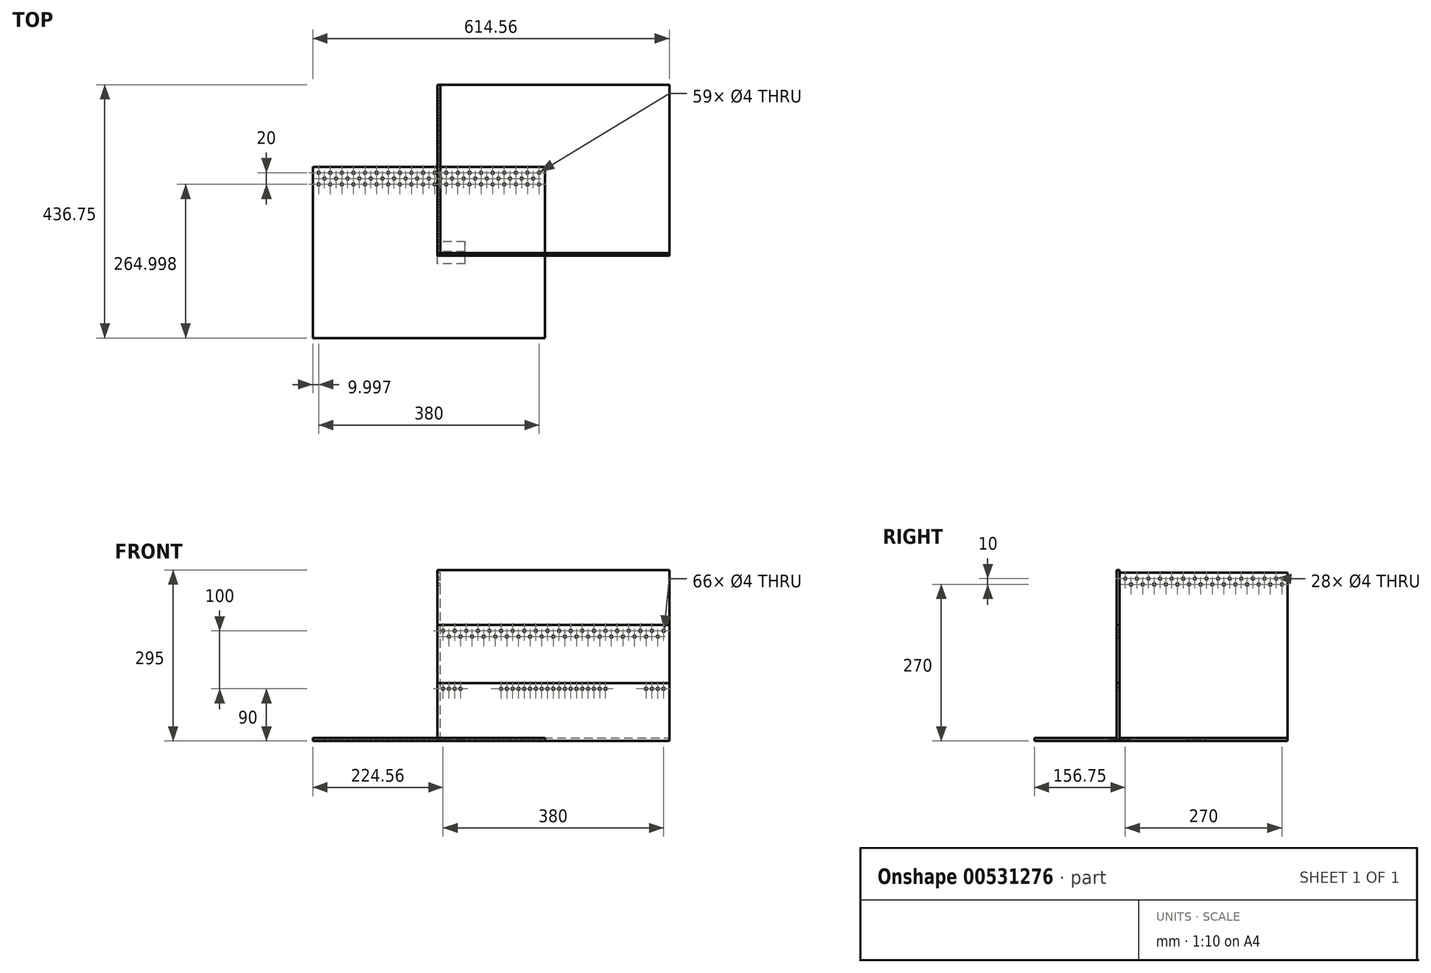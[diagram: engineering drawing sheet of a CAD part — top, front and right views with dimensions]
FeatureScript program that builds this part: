
annotation { "Feature Type Name" : "Feature", "Feature Type Description" : "" }
export const myFeature = defineFeature(function(context is Context, id is Id, definition is map)
    precondition{}
    {
        {
            var Q0;
            Q0=qCreatedBy(makeId("Front.planeOp"),FACE);
            var sketch = newSketch(context, id + "F0", { "sketchPlane" : qUnion([Q0])});
            skLineSegment(sketch, "E0.bottom", {"start": v(0, 0) * mm, "end": v(400, 0) * mm});
            skLineSegment(sketch, "E0.top", {"start": v(0, 100) * mm, "end": v(400, 100) * mm});
            skLineSegment(sketch, "E0.left", {"start": v(0, 0) * mm, "end": v(0, 100) * mm});
            skLineSegment(sketch, "E0.right", {"start": v(400, 0) * mm, "end": v(400, 100) * mm});
            skCircle(sketch, "E1", {"center": v(10, 90) * mm, "radius": 2 * mm});
            skCircle(sketch, "E2.1.0.0", {"center": v(20, 90) * mm, "radius": 2 * mm});
            skCircle(sketch, "E2.2.0.0", {"center": v(30, 90) * mm, "radius": 2 * mm});
            skCircle(sketch, "E2.3.0.0", {"center": v(40, 90) * mm, "radius": 2 * mm});
            skCircle(sketch, "E2.10.0.0", {"center": v(110, 90) * mm, "radius": 2 * mm});
            skCircle(sketch, "E2.11.0.0", {"center": v(120, 90) * mm, "radius": 2 * mm});
            skCircle(sketch, "E2.12.0.0", {"center": v(130, 90) * mm, "radius": 2 * mm});
            skCircle(sketch, "E2.13.0.0", {"center": v(140, 90) * mm, "radius": 2 * mm});
            skCircle(sketch, "E2.14.0.0", {"center": v(150, 90) * mm, "radius": 2 * mm});
            skCircle(sketch, "E2.15.0.0", {"center": v(160, 90) * mm, "radius": 2 * mm});
            skCircle(sketch, "E2.16.0.0", {"center": v(170, 90) * mm, "radius": 2 * mm});
            skCircle(sketch, "E2.17.0.0", {"center": v(180, 90) * mm, "radius": 2 * mm});
            skCircle(sketch, "E2.18.0.0", {"center": v(190, 90) * mm, "radius": 2 * mm});
            skCircle(sketch, "E2.19.0.0", {"center": v(200, 90) * mm, "radius": 2 * mm});
            skCircle(sketch, "E2.20.0.0", {"center": v(210, 90) * mm, "radius": 2 * mm});
            skCircle(sketch, "E2.21.0.0", {"center": v(220, 90) * mm, "radius": 2 * mm});
            skCircle(sketch, "E2.22.0.0", {"center": v(230, 90) * mm, "radius": 2 * mm});
            skCircle(sketch, "E2.23.0.0", {"center": v(240, 90) * mm, "radius": 2 * mm});
            skCircle(sketch, "E2.24.0.0", {"center": v(250, 90) * mm, "radius": 2 * mm});
            skCircle(sketch, "E2.25.0.0", {"center": v(260, 90) * mm, "radius": 2 * mm});
            skCircle(sketch, "E2.26.0.0", {"center": v(270, 90) * mm, "radius": 2 * mm});
            skCircle(sketch, "E2.27.0.0", {"center": v(280, 90) * mm, "radius": 2 * mm});
            skCircle(sketch, "E2.28.0.0", {"center": v(290, 90) * mm, "radius": 2 * mm});
            skCircle(sketch, "E2.35.0.0", {"center": v(360, 90) * mm, "radius": 2 * mm});
            skCircle(sketch, "E2.36.0.0", {"center": v(370, 90) * mm, "radius": 2 * mm});
            skCircle(sketch, "E2.37.0.0", {"center": v(380, 90) * mm, "radius": 2 * mm});
            skCircle(sketch, "E2.38.0.0", {"center": v(390, 90) * mm, "radius": 2 * mm});
            skLineSegment(sketch, "E2.direction1", {"start": v(10, 90) * mm, "end": v(20, 90) * mm, "construction": true});
            skLineSegment(sketch, "E3.top", {"start": v(50, 81) * mm, "end": v(95, 81) * mm, "construction": true});
            skLineSegment(sketch, "E3.left", {"start": v(50, 100) * mm, "end": v(50, 81) * mm, "construction": true});
            skLineSegment(sketch, "E3.right", {"start": v(95, 100) * mm, "end": v(95, 81) * mm, "construction": true});
            skLineSegment(sketch, "E4.top", {"start": v(350, 81) * mm, "end": v(305, 81) * mm, "construction": true});
            skLineSegment(sketch, "E4.left", {"start": v(350, 100) * mm, "end": v(350, 81) * mm, "construction": true});
            skLineSegment(sketch, "E4.right", {"start": v(305, 100) * mm, "end": v(305, 81) * mm, "construction": true});
            skSolve(sketch);
        }
        {
            var Q0;
            Q0=makeQuery(id+"F0.imprint","IMPRINT",FACE,{"disambiguationData":[TD([[makeQuery(id+"F0.imprint","IMPRINT",EDGE,{"derivedFrom":sQuery(id+"F0.wireOp",EDGE,"E0.bottom")}),1.0]])]});
            extrude(context, id + "F1", {"entities" : qUnion([Q0]), "depth" : 5 * mm, "offsetDistance" : 25 * mm});
        }
        {
            var Q0;
            Q0=qCreatedBy(makeId("Front.planeOp"),FACE);
            var sketch = newSketch(context, id + "F2", { "sketchPlane" : qUnion([Q0])});
            skLineSegment(sketch, "E5.bottom", {"start": v(0, 0) * mm, "end": v(400, 0) * mm});
            skLineSegment(sketch, "E5.top", {"start": v(0, 200) * mm, "end": v(400, 200) * mm});
            skLineSegment(sketch, "E5.left", {"start": v(0, 0) * mm, "end": v(0, 200) * mm});
            skLineSegment(sketch, "E5.right", {"start": v(400, 0) * mm, "end": v(400, 200) * mm});
            skCircle(sketch, "E6", {"center": v(10, 190) * mm, "radius": 2 * mm});
            skCircle(sketch, "E7", {"center": v(20, 180) * mm, "radius": 2 * mm});
            skCircle(sketch, "E8.1.0.0", {"center": v(30, 190) * mm, "radius": 2 * mm});
            skCircle(sketch, "E8.2.0.0", {"center": v(50, 190) * mm, "radius": 2 * mm});
            skCircle(sketch, "E8.3.0.0", {"center": v(70, 190) * mm, "radius": 2 * mm});
            skCircle(sketch, "E8.4.0.0", {"center": v(90, 190) * mm, "radius": 2 * mm});
            skCircle(sketch, "E8.5.0.0", {"center": v(110, 190) * mm, "radius": 2 * mm});
            skCircle(sketch, "E8.6.0.0", {"center": v(130, 190) * mm, "radius": 2 * mm});
            skCircle(sketch, "E8.7.0.0", {"center": v(150, 190) * mm, "radius": 2 * mm});
            skCircle(sketch, "E8.8.0.0", {"center": v(170, 190) * mm, "radius": 2 * mm});
            skCircle(sketch, "E8.9.0.0", {"center": v(190, 190) * mm, "radius": 2 * mm});
            skCircle(sketch, "E8.10.0.0", {"center": v(210, 190) * mm, "radius": 2 * mm});
            skCircle(sketch, "E8.11.0.0", {"center": v(230, 190) * mm, "radius": 2 * mm});
            skCircle(sketch, "E8.12.0.0", {"center": v(250, 190) * mm, "radius": 2 * mm});
            skCircle(sketch, "E8.13.0.0", {"center": v(270, 190) * mm, "radius": 2 * mm});
            skCircle(sketch, "E8.14.0.0", {"center": v(290, 190) * mm, "radius": 2 * mm});
            skCircle(sketch, "E8.15.0.0", {"center": v(310, 190) * mm, "radius": 2 * mm});
            skCircle(sketch, "E8.16.0.0", {"center": v(330, 190) * mm, "radius": 2 * mm});
            skCircle(sketch, "E8.17.0.0", {"center": v(350, 190) * mm, "radius": 2 * mm});
            skCircle(sketch, "E8.18.0.0", {"center": v(370, 190) * mm, "radius": 2 * mm});
            skCircle(sketch, "E8.19.0.0", {"center": v(390, 190) * mm, "radius": 2 * mm});
            skLineSegment(sketch, "E8.direction1", {"start": v(10, 190) * mm, "end": v(30, 190) * mm, "construction": true});
            skCircle(sketch, "E9.1.0.0", {"center": v(40, 180) * mm, "radius": 2 * mm});
            skCircle(sketch, "E9.2.0.0", {"center": v(60, 180) * mm, "radius": 2 * mm});
            skCircle(sketch, "E9.3.0.0", {"center": v(80, 180) * mm, "radius": 2 * mm});
            skCircle(sketch, "E9.4.0.0", {"center": v(100, 180) * mm, "radius": 2 * mm});
            skCircle(sketch, "E9.5.0.0", {"center": v(120, 180) * mm, "radius": 2 * mm});
            skCircle(sketch, "E9.6.0.0", {"center": v(140, 180) * mm, "radius": 2 * mm});
            skCircle(sketch, "E9.7.0.0", {"center": v(160, 180) * mm, "radius": 2 * mm});
            skCircle(sketch, "E9.8.0.0", {"center": v(180, 180) * mm, "radius": 2 * mm});
            skCircle(sketch, "E9.9.0.0", {"center": v(200, 180) * mm, "radius": 2 * mm});
            skCircle(sketch, "E9.10.0.0", {"center": v(220, 180) * mm, "radius": 2 * mm});
            skCircle(sketch, "E9.11.0.0", {"center": v(240, 180) * mm, "radius": 2 * mm});
            skCircle(sketch, "E9.12.0.0", {"center": v(260, 180) * mm, "radius": 2 * mm});
            skCircle(sketch, "E9.13.0.0", {"center": v(280, 180) * mm, "radius": 2 * mm});
            skCircle(sketch, "E9.14.0.0", {"center": v(300, 180) * mm, "radius": 2 * mm});
            skCircle(sketch, "E9.15.0.0", {"center": v(320, 180) * mm, "radius": 2 * mm});
            skCircle(sketch, "E9.16.0.0", {"center": v(340, 180) * mm, "radius": 2 * mm});
            skCircle(sketch, "E9.17.0.0", {"center": v(360, 180) * mm, "radius": 2 * mm});
            skCircle(sketch, "E9.18.0.0", {"center": v(380, 180) * mm, "radius": 2 * mm});
            skLineSegment(sketch, "E9.direction1", {"start": v(20, 180) * mm, "end": v(40, 180) * mm, "construction": true});
            skSolve(sketch);
        }
        {
            var Q0;
            Q0 = qSketchRegion(id + "F2", true);
            extrude(context, id + "F3", {"entities" : qUnion([Q0]), "depth" : 5 * mm, "offsetDistance" : 25 * mm});
        }
        {
            var Q0;
            Q0=qCreatedBy(makeId("Right.planeOp"),FACE);
            var sketch = newSketch(context, id + "F4", { "sketchPlane" : qUnion([Q0])});
            skLineSegment(sketch, "E10.bottom", {"start": v(0, 0) * mm, "end": v(290, 0) * mm});
            skLineSegment(sketch, "E10.top", {"start": v(0, 290) * mm, "end": v(290, 290) * mm});
            skLineSegment(sketch, "E10.left", {"start": v(0, 0) * mm, "end": v(0, 290) * mm});
            skLineSegment(sketch, "E10.right", {"start": v(290, 0) * mm, "end": v(290, 290) * mm});
            skCircle(sketch, "E11", {"center": v(10, 280) * mm, "radius": 2 * mm});
            skCircle(sketch, "E12", {"center": v(20, 270) * mm, "radius": 2 * mm});
            skCircle(sketch, "E13.1.0.0", {"center": v(30, 280) * mm, "radius": 2 * mm});
            skCircle(sketch, "E13.2.0.0", {"center": v(50, 280) * mm, "radius": 2 * mm});
            skCircle(sketch, "E13.3.0.0", {"center": v(70, 280) * mm, "radius": 2 * mm});
            skCircle(sketch, "E13.4.0.0", {"center": v(90, 280) * mm, "radius": 2 * mm});
            skCircle(sketch, "E13.5.0.0", {"center": v(110, 280) * mm, "radius": 2 * mm});
            skCircle(sketch, "E13.6.0.0", {"center": v(130, 280) * mm, "radius": 2 * mm});
            skCircle(sketch, "E13.7.0.0", {"center": v(150, 280) * mm, "radius": 2 * mm});
            skCircle(sketch, "E13.8.0.0", {"center": v(170, 280) * mm, "radius": 2 * mm});
            skCircle(sketch, "E13.9.0.0", {"center": v(190, 280) * mm, "radius": 2 * mm});
            skCircle(sketch, "E13.10.0.0", {"center": v(210, 280) * mm, "radius": 2 * mm});
            skCircle(sketch, "E13.11.0.0", {"center": v(230, 280) * mm, "radius": 2 * mm});
            skCircle(sketch, "E13.12.0.0", {"center": v(250, 280) * mm, "radius": 2 * mm});
            skCircle(sketch, "E13.13.0.0", {"center": v(270, 280) * mm, "radius": 2 * mm});
            skLineSegment(sketch, "E13.direction1", {"start": v(10, 280) * mm, "end": v(30, 280) * mm, "construction": true});
            skCircle(sketch, "E14.1.0.0", {"center": v(40, 270) * mm, "radius": 2 * mm});
            skCircle(sketch, "E14.2.0.0", {"center": v(60, 270) * mm, "radius": 2 * mm});
            skCircle(sketch, "E14.3.0.0", {"center": v(80, 270) * mm, "radius": 2 * mm});
            skCircle(sketch, "E14.4.0.0", {"center": v(100, 270) * mm, "radius": 2 * mm});
            skCircle(sketch, "E14.5.0.0", {"center": v(120, 270) * mm, "radius": 2 * mm});
            skCircle(sketch, "E14.6.0.0", {"center": v(140, 270) * mm, "radius": 2 * mm});
            skCircle(sketch, "E14.7.0.0", {"center": v(160, 270) * mm, "radius": 2 * mm});
            skCircle(sketch, "E14.8.0.0", {"center": v(180, 270) * mm, "radius": 2 * mm});
            skCircle(sketch, "E14.9.0.0", {"center": v(200, 270) * mm, "radius": 2 * mm});
            skCircle(sketch, "E14.10.0.0", {"center": v(220, 270) * mm, "radius": 2 * mm});
            skCircle(sketch, "E14.11.0.0", {"center": v(240, 270) * mm, "radius": 2 * mm});
            skCircle(sketch, "E14.12.0.0", {"center": v(260, 270) * mm, "radius": 2 * mm});
            skCircle(sketch, "E14.13.0.0", {"center": v(280, 270) * mm, "radius": 2 * mm});
            skLineSegment(sketch, "E14.direction1", {"start": v(20, 270) * mm, "end": v(40, 270) * mm, "construction": true});
            skSolve(sketch);
        }
        {
            var Q0;
            Q0 = qSketchRegion(id + "F4", true);
            extrude(context, id + "F5", {"entities" : qUnion([Q0]), "depth" : 5 * mm, "offsetDistance" : 25 * mm});
        }
        {
            var Q0;
            Q0=qCreatedBy(makeId("Top.planeOp"),FACE);
            var sketch = newSketch(context, id + "F6", { "sketchPlane" : qUnion([Q0])});
            skLineSegment(sketch, "E15.bottom", {"start": v(0, 0) * mm, "end": v(400, 0) * mm});
            skLineSegment(sketch, "E15.top", {"start": v(0, 290) * mm, "end": v(400, 290) * mm});
            skLineSegment(sketch, "E15.left", {"start": v(0, 0) * mm, "end": v(0, 290) * mm});
            skLineSegment(sketch, "E15.right", {"start": v(400, 0) * mm, "end": v(400, 290) * mm});
            skSolve(sketch);
        }
        {
            var Q0;
            Q0 = qSketchRegion(id + "F6", true);
            extrude(context, id + "F7", {"entities" : qUnion([Q0]), "depth" : 5 * mm, "offsetDistance" : 25 * mm});
        }
        {
            var Q0;
            Q0=qCreatedBy(makeId("Front.planeOp"),FACE);
            var sketch = newSketch(context, id + "F8", { "sketchPlane" : qUnion([Q0])});
            skLineSegment(sketch, "E16.bottom", {"start": v(0, 0) * mm, "end": v(400, 0) * mm});
            skLineSegment(sketch, "E16.top", {"start": v(0, 295) * mm, "end": v(400, 295) * mm});
            skLineSegment(sketch, "E16.left", {"start": v(0, 0) * mm, "end": v(0, 295) * mm});
            skLineSegment(sketch, "E16.right", {"start": v(400, 0) * mm, "end": v(400, 295) * mm});
            skSolve(sketch);
        }
        {
            var Q0;
            Q0 = qSketchRegion(id + "F8", true);
            extrude(context, id + "F9", {"entities" : qUnion([Q0]), "depth" : 5 * mm, "offsetDistance" : 25 * mm});
        }
        {
            var Q0;
            Q0=qCreatedBy(makeId("Top.planeOp"),FACE);
            var sketch = newSketch(context, id + "F10", { "sketchPlane" : qUnion([Q0])});
            skLineSegment(sketch, "E17.bottom", {"start": v(-214.56, 148.25) * mm, "end": v(185.44, 148.25) * mm});
            skLineSegment(sketch, "E17.top", {"start": v(-214.56, -146.75) * mm, "end": v(185.44, -146.75) * mm});
            skLineSegment(sketch, "E17.left", {"start": v(-214.56, 148.25) * mm, "end": v(-214.56, -146.75) * mm});
            skLineSegment(sketch, "E17.right", {"start": v(185.44, 148.25) * mm, "end": v(185.44, -146.75) * mm});
            skCircle(sketch, "E18", {"center": v(-204.56, 138.25) * mm, "radius": 2 * mm});
            skCircle(sketch, "E19", {"center": v(-194.56, 128.25) * mm, "radius": 2 * mm});
            skCircle(sketch, "E20.1.0.0", {"center": v(-184.56, 138.25) * mm, "radius": 2 * mm});
            skCircle(sketch, "E20.2.0.0", {"center": v(-164.56, 138.25) * mm, "radius": 2 * mm});
            skCircle(sketch, "E20.3.0.0", {"center": v(-144.56, 138.25) * mm, "radius": 2 * mm});
            skCircle(sketch, "E20.4.0.0", {"center": v(-124.56, 138.25) * mm, "radius": 2 * mm});
            skCircle(sketch, "E20.5.0.0", {"center": v(-104.56, 138.25) * mm, "radius": 2 * mm});
            skCircle(sketch, "E20.6.0.0", {"center": v(-84.56, 138.25) * mm, "radius": 2 * mm});
            skCircle(sketch, "E20.7.0.0", {"center": v(-64.56, 138.25) * mm, "radius": 2 * mm});
            skCircle(sketch, "E20.8.0.0", {"center": v(-44.56, 138.25) * mm, "radius": 2 * mm});
            skCircle(sketch, "E20.9.0.0", {"center": v(-24.56, 138.25) * mm, "radius": 2 * mm});
            skCircle(sketch, "E20.10.0.0", {"center": v(-4.56, 138.25) * mm, "radius": 2 * mm});
            skCircle(sketch, "E20.11.0.0", {"center": v(15.44, 138.25) * mm, "radius": 2 * mm});
            skCircle(sketch, "E20.12.0.0", {"center": v(35.44, 138.25) * mm, "radius": 2 * mm});
            skCircle(sketch, "E20.13.0.0", {"center": v(55.44, 138.25) * mm, "radius": 2 * mm});
            skCircle(sketch, "E20.14.0.0", {"center": v(75.44, 138.25) * mm, "radius": 2 * mm});
            skLineSegment(sketch, "E20.direction1", {"start": v(-204.56, 138.25) * mm, "end": v(-184.56, 138.25) * mm, "construction": true});
            skCircle(sketch, "E21.1.0.0", {"center": v(-174.56, 128.25) * mm, "radius": 2 * mm});
            skCircle(sketch, "E21.2.0.0", {"center": v(-154.56, 128.25) * mm, "radius": 2 * mm});
            skCircle(sketch, "E21.3.0.0", {"center": v(-134.56, 128.25) * mm, "radius": 2 * mm});
            skCircle(sketch, "E21.4.0.0", {"center": v(-114.56, 128.25) * mm, "radius": 2 * mm});
            skCircle(sketch, "E21.5.0.0", {"center": v(-94.56, 128.25) * mm, "radius": 2 * mm});
            skCircle(sketch, "E21.6.0.0", {"center": v(-74.56, 128.25) * mm, "radius": 2 * mm});
            skCircle(sketch, "E21.7.0.0", {"center": v(-54.56, 128.25) * mm, "radius": 2 * mm});
            skCircle(sketch, "E21.8.0.0", {"center": v(-34.56, 128.25) * mm, "radius": 2 * mm});
            skCircle(sketch, "E21.9.0.0", {"center": v(-14.56, 128.25) * mm, "radius": 2 * mm});
            skCircle(sketch, "E21.10.0.0", {"center": v(5.44, 128.25) * mm, "radius": 2 * mm});
            skCircle(sketch, "E21.11.0.0", {"center": v(25.44, 128.25) * mm, "radius": 2 * mm});
            skCircle(sketch, "E21.12.0.0", {"center": v(45.44, 128.25) * mm, "radius": 2 * mm});
            skCircle(sketch, "E21.13.0.0", {"center": v(65.44, 128.25) * mm, "radius": 2 * mm});
            skLineSegment(sketch, "E21.direction1", {"start": v(-194.56, 128.25) * mm, "end": v(-174.56, 128.25) * mm, "construction": true});
            skCircle(sketch, "E22.0.15.0", {"center": v(95.44, 138.25) * mm, "radius": 2 * mm});
            skCircle(sketch, "E22.0.16.0", {"center": v(115.44, 138.25) * mm, "radius": 2 * mm});
            skCircle(sketch, "E22.0.17.0", {"center": v(135.44, 138.25) * mm, "radius": 2 * mm});
            skCircle(sketch, "E22.0.18.0", {"center": v(155.44, 138.25) * mm, "radius": 2 * mm});
            skCircle(sketch, "E22.0.19.0", {"center": v(175.44, 138.25) * mm, "radius": 2 * mm});
            skCircle(sketch, "E23.0.14.0", {"center": v(85.44, 128.25) * mm, "radius": 2 * mm});
            skCircle(sketch, "E23.0.15.0", {"center": v(105.44, 128.25) * mm, "radius": 2 * mm});
            skCircle(sketch, "E23.0.16.0", {"center": v(125.44, 128.25) * mm, "radius": 2 * mm});
            skCircle(sketch, "E23.0.17.0", {"center": v(145.44, 128.25) * mm, "radius": 2 * mm});
            skCircle(sketch, "E23.0.18.0", {"center": v(165.44, 128.25) * mm, "radius": 2 * mm});
            skCircle(sketch, "E24", {"center": v(-204.56, 118.25) * mm, "radius": 2 * mm});
            skCircle(sketch, "E25.1.0.0", {"center": v(-184.56, 118.25) * mm, "radius": 2 * mm});
            skCircle(sketch, "E25.2.0.0", {"center": v(-164.56, 118.25) * mm, "radius": 2 * mm});
            skCircle(sketch, "E25.3.0.0", {"center": v(-144.56, 118.25) * mm, "radius": 2 * mm});
            skCircle(sketch, "E25.4.0.0", {"center": v(-124.56, 118.25) * mm, "radius": 2 * mm});
            skCircle(sketch, "E25.5.0.0", {"center": v(-104.56, 118.25) * mm, "radius": 2 * mm});
            skCircle(sketch, "E25.6.0.0", {"center": v(-84.56, 118.25) * mm, "radius": 2 * mm});
            skCircle(sketch, "E25.7.0.0", {"center": v(-64.56, 118.25) * mm, "radius": 2 * mm});
            skCircle(sketch, "E25.8.0.0", {"center": v(-44.56, 118.25) * mm, "radius": 2 * mm});
            skCircle(sketch, "E25.9.0.0", {"center": v(-24.56, 118.25) * mm, "radius": 2 * mm});
            skCircle(sketch, "E25.10.0.0", {"center": v(-4.56, 118.25) * mm, "radius": 2 * mm});
            skCircle(sketch, "E25.11.0.0", {"center": v(15.44, 118.25) * mm, "radius": 2 * mm});
            skCircle(sketch, "E25.12.0.0", {"center": v(35.44, 118.25) * mm, "radius": 2 * mm});
            skCircle(sketch, "E25.13.0.0", {"center": v(55.44, 118.25) * mm, "radius": 2 * mm});
            skCircle(sketch, "E25.14.0.0", {"center": v(75.44, 118.25) * mm, "radius": 2 * mm});
            skCircle(sketch, "E25.15.0.0", {"center": v(95.44, 118.25) * mm, "radius": 2 * mm});
            skCircle(sketch, "E25.16.0.0", {"center": v(115.44, 118.25) * mm, "radius": 2 * mm});
            skCircle(sketch, "E25.17.0.0", {"center": v(135.44, 118.25) * mm, "radius": 2 * mm});
            skCircle(sketch, "E25.18.0.0", {"center": v(155.44, 118.25) * mm, "radius": 2 * mm});
            skCircle(sketch, "E25.19.0.0", {"center": v(175.44, 118.25) * mm, "radius": 2 * mm});
            skLineSegment(sketch, "E25.direction1", {"start": v(-204.56, 118.25) * mm, "end": v(-184.56, 118.25) * mm, "construction": true});
            skSolve(sketch);
        }
        {
            var Q0;
            Q0 = qSketchRegion(id + "F10", true);
            extrude(context, id + "F11", {"entities" : qUnion([Q0]), "depth" : 5 * mm, "offsetDistance" : 25 * mm});
        }
        {
            var Q0;
            Q0=qCreatedBy(makeId("Right.planeOp"),FACE);
            var sketch = newSketch(context, id + "F12", { "sketchPlane" : qUnion([Q0])});
            skLineSegment(sketch, "E26.bottom", {"start": v(-18.4, 0) * mm, "end": v(19.6, 0) * mm});
            skLineSegment(sketch, "E26.top", {"start": v(-12.66, 3) * mm, "end": v(-2.3, 3) * mm});
            skLineSegment(sketch, "E26.left", {"start": v(-18.4, 0) * mm, "end": v(-18.4, 0.76) * mm});
            skLineSegment(sketch, "E26.right", {"start": v(19.6, 0) * mm, "end": v(19.6, 0.76) * mm});
            skArc(sketch, "E27.trimOffspring", {"start": v(2.3, 3) * mm, "mid": v(0, 4.5) * mm, "end": v(-2.3, 3) * mm});
            skLineSegment(sketch, "E28", {"start": v(-17.68, 1.71) * mm, "end": v(-14.1, 2.79) * mm});
            skLineSegment(sketch, "E29", {"start": v(18.9, 1.71) * mm, "end": v(15.31, 2.79) * mm});
            skPoint(sketch, "E30.orphan", {"position": v(19.6, 3) * mm});
            skPoint(sketch, "E31.orphan", {"position": v(-18.4, 3) * mm});
            skPoint(sketch, "E32.visualSharp", {"position": v(-18.4, 1.5) * mm});
            skArc(sketch, "E32.filletArc", {"start": v(-17.68, 1.71) * mm, "mid": v(-18.2, 1.35) * mm, "end": v(-18.4, 0.76) * mm});
            skPoint(sketch, "E33.visualSharp", {"position": v(19.6, 1.5) * mm});
            skArc(sketch, "E33.filletArc", {"start": v(19.6, 0.76) * mm, "mid": v(19.4, 1.35) * mm, "end": v(18.9, 1.71) * mm});
            skPoint(sketch, "E34.visualSharp", {"position": v(-13.4, 3) * mm});
            skArc(sketch, "E34.filletArc", {"start": v(-12.66, 3) * mm, "mid": v(-13.38, 2.95) * mm, "end": v(-14.1, 2.79) * mm});
            skPoint(sketch, "E35.visualSharp", {"position": v(14.6, 3) * mm});
            skArc(sketch, "E35.filletArc", {"start": v(15.31, 2.79) * mm, "mid": v(14.6, 2.95) * mm, "end": v(13.87, 3) * mm});
            skLineSegment(sketch, "E36.trimOffspring", {"start": v(2.3, 3) * mm, "end": v(13.87, 3) * mm});
            skSolve(sketch);
        }
        {
            var Q0;
            Q0 = qSketchRegion(id + "F12", true);
            extrude(context, id + "F13", {"entities" : qUnion([Q0]), "depth" : 48 * mm, "offsetDistance" : 25 * mm});
        }
    });
